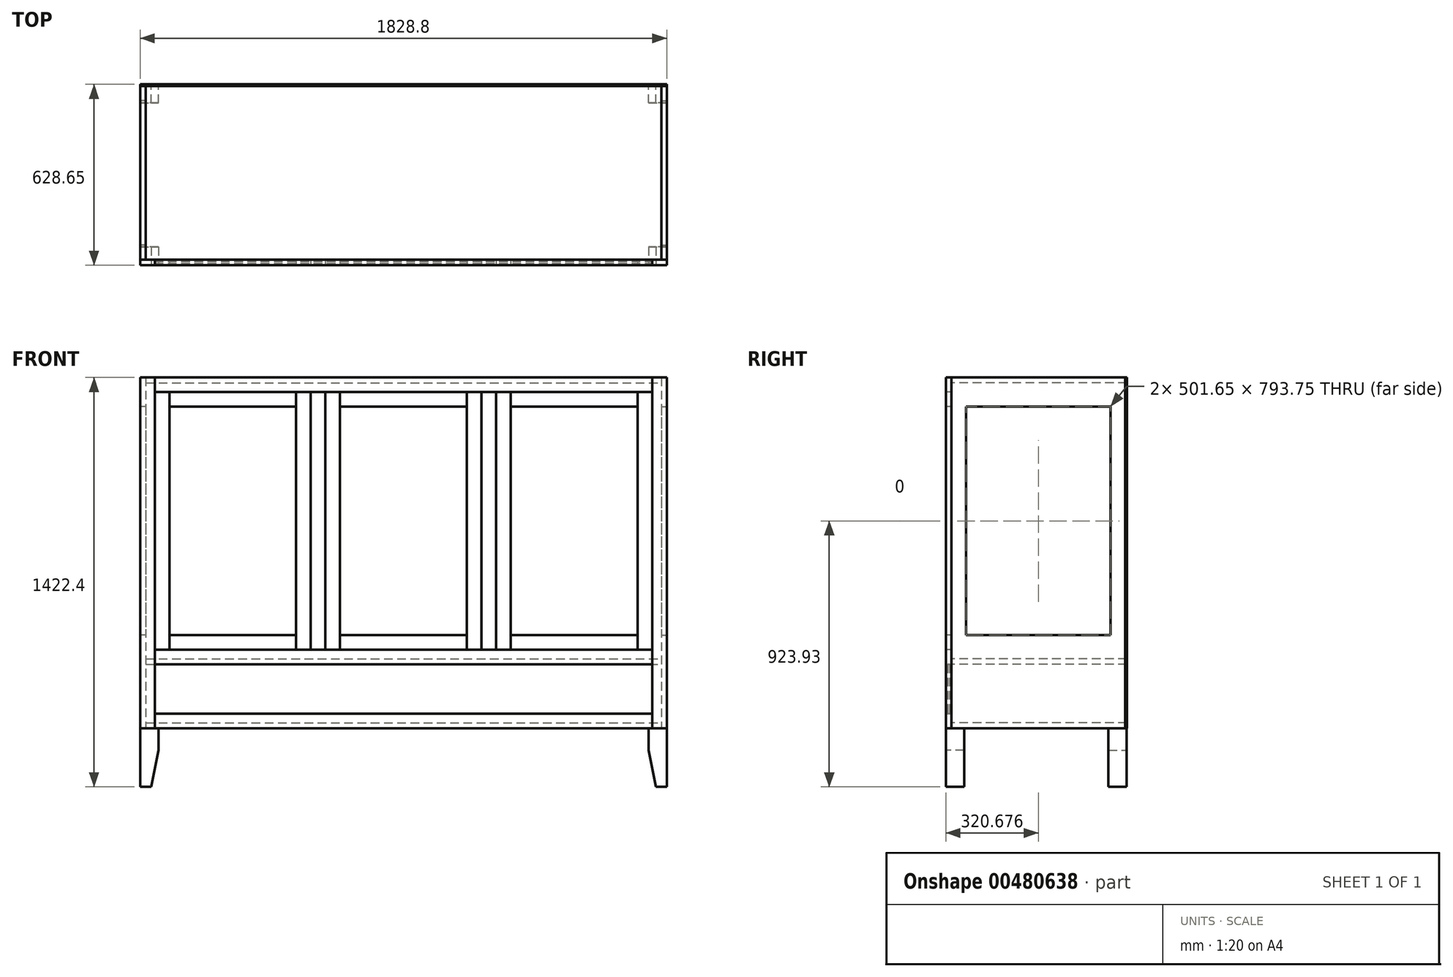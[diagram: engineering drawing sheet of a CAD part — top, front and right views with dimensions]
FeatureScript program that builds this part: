
annotation { "Feature Type Name" : "Feature", "Feature Type Description" : "" }
export const myFeature = defineFeature(function(context is Context, id is Id, definition is map)
    precondition{}
    {
        {
            var Q0;
            Q0=qCreatedBy(makeId("Right.planeOp"),FACE);
            var sketch = newSketch(context, id + "F0", { "sketchPlane" : qUnion([Q0])});
            skLineSegment(sketch, "E0.bottom", {"start": v(-30.46, 1128.18) * mm, "end": v(579.14, 1128.18) * mm});
            skLineSegment(sketch, "E0.top", {"start": v(-30.46, -91.02) * mm, "end": v(579.14, -91.02) * mm});
            skLineSegment(sketch, "E0.left", {"start": v(-30.46, 1128.18) * mm, "end": v(-30.46, -91.02) * mm});
            skLineSegment(sketch, "E0.right", {"start": v(579.14, 1128.18) * mm, "end": v(579.14, -91.02) * mm});
            skSolve(sketch);
        }
        {
            var Q0;
            Q0=qSketchRegion(id+"F0",true);
            extrude(context, id + "F1", {"entities" : qUnion([Q0]), "depth" : 19.05 * mm});
        }
        {
            var Q0;
            Q0=makeQuery(id+"F1.opExtrude","CAP_FACE",FACE,{"disambiguationData":[OSD([sQuery(id+"F0.wireOp",EDGE,"E0.bottom"),sQuery(id+"F0.wireOp",EDGE,"E0.top"),sQuery(id+"F0.wireOp",EDGE,"E0.left"),sQuery(id+"F0.wireOp",EDGE,"E0.right")])],"isStart":false});
            var sketch = newSketch(context, id + "F2", { "sketchPlane" : qUnion([Q0])});
            skLineSegment(sketch, "E1.bottom", {"start": v(20.34, 1026.58) * mm, "end": v(522, 1026.58) * mm});
            skLineSegment(sketch, "E1.top", {"start": v(20.34, 232.83) * mm, "end": v(522, 232.83) * mm});
            skLineSegment(sketch, "E1.left", {"start": v(20.34, 1026.58) * mm, "end": v(20.34, 232.83) * mm});
            skLineSegment(sketch, "E1.right", {"start": v(522, 1026.58) * mm, "end": v(522, 232.83) * mm});
            skSolve(sketch);
        }
        {
            var Q0;
            Q0 = qSketchRegion(id + "F2", true);
            extrude(context, id + "F3", {"entities" : qUnion([Q0]), "operationType" : NewBodyOperationType.REMOVE, "endBound" : BoundingType.THROUGH_ALL, "oppositeDirection" : true, "depth" : 2032 * mm});
        }
        {
            var Q0;
            Q0=makeQuery(id+"F1.opExtrude","CAP_FACE",FACE,{"disambiguationData":[OSD([sQuery(id+"F0.wireOp",EDGE,"E0.bottom"),sQuery(id+"F0.wireOp",EDGE,"E0.top"),sQuery(id+"F0.wireOp",EDGE,"E0.left"),sQuery(id+"F0.wireOp",EDGE,"E0.right")])],"isStart":false});
            cPlane(context, id + "F4", {"entities" : qUnion([Q0]), "cplaneType" : CPlaneType.OFFSET, "offset" : 914.4 * mm, "oppositeDirection" : true, "width" : 152.4 * mm, "height" : 152.4 * mm});
        }
        {
            var Q0;
            Q0=makeQuery(id+"F1.opExtrude","SWEPT_BODY",BODY,{"disambiguationData":[OSD([sQuery(id+"F0.wireOp",EDGE,"E0.bottom"),sQuery(id+"F0.wireOp",EDGE,"E0.top"),sQuery(id+"F0.wireOp",EDGE,"E0.left"),sQuery(id+"F0.wireOp",EDGE,"E0.right")])]});
            var Q1;
            Q1=qCreatedBy(id+"F4.planeOp",FACE);
            mirror(context, id + "F5", {"entities" : qUnion([Q0]), "mirrorPlane" : qUnion([Q1])});
        }
        {
            var Q0;
            Q0=makeQuery(id+"F1.opExtrude","SWEPT_FACE",FACE,{"disambiguationData":[OSD([sQuery(id+"F0.wireOp",EDGE,"E0.left")])]});
            var sketch = newSketch(context, id + "F6", { "sketchPlane" : qUnion([Q0])});
            skLineSegment(sketch, "E2.bottom", {"start": v(-1790.7, 1128.18) * mm, "end": v(0, 1128.18) * mm});
            skLineSegment(sketch, "E2.top", {"start": v(-1790.7, 1109.13) * mm, "end": v(0, 1109.13) * mm});
            skLineSegment(sketch, "E2.left", {"start": v(-1790.7, 1128.18) * mm, "end": v(-1790.7, 1109.13) * mm});
            skLineSegment(sketch, "E2.right", {"start": v(0, 1128.18) * mm, "end": v(0, 1109.13) * mm});
            skSolve(sketch);
        }
        {
            var Q0;
            Q0=qSketchRegion(id+"F6",true);
            extrude(context, id + "F7", {"entities" : qUnion([Q0]), "oppositeDirection" : true, "depth" : 609.6 * mm});
        }
        {
            var Q0;
            Q0=makeQuery(id+"F1.opExtrude","SWEPT_FACE",FACE,{"disambiguationData":[OSD([sQuery(id+"F0.wireOp",EDGE,"E0.left")])]});
            var sketch = newSketch(context, id + "F8", { "sketchPlane" : qUnion([Q0])});
            skLineSegment(sketch, "E3.bottom", {"start": v(-1790.7, -71.97) * mm, "end": v(0, -71.97) * mm});
            skLineSegment(sketch, "E3.top", {"start": v(-1790.7, -91.02) * mm, "end": v(0, -91.02) * mm});
            skLineSegment(sketch, "E3.left", {"start": v(-1790.7, -71.97) * mm, "end": v(-1790.7, -91.02) * mm});
            skLineSegment(sketch, "E3.right", {"start": v(0, -71.97) * mm, "end": v(0, -91.02) * mm});
            skSolve(sketch);
        }
        {
            var Q0;
            Q0=qSketchRegion(id+"F8",true);
            extrude(context, id + "F9", {"entities" : qUnion([Q0]), "oppositeDirection" : true, "depth" : 609.6 * mm});
        }
        {
            var Q0;
            Q0=makeQuery(id+"F1.opExtrude","SWEPT_FACE",FACE,{"disambiguationData":[OSD([sQuery(id+"F0.wireOp",EDGE,"E0.left")])]});
            var sketch = newSketch(context, id + "F10", { "sketchPlane" : qUnion([Q0])});
            skLineSegment(sketch, "E4.bottom", {"start": v(-1790.7, 150.28) * mm, "end": v(0, 150.28) * mm});
            skLineSegment(sketch, "E4.top", {"start": v(-1790.7, 131.23) * mm, "end": v(0, 131.23) * mm});
            skLineSegment(sketch, "E4.left", {"start": v(-1790.7, 150.28) * mm, "end": v(-1790.7, 131.23) * mm});
            skLineSegment(sketch, "E4.right", {"start": v(0, 150.28) * mm, "end": v(0, 131.23) * mm});
            skSolve(sketch);
        }
        {
            var Q0;
            Q0=qSketchRegion(id+"F10",true);
            extrude(context, id + "F11", {"entities" : qUnion([Q0]), "oppositeDirection" : true, "depth" : 609.6 * mm});
        }
        {
            var Q0;
            Q0=makeQuery(id+"F1.opExtrude","SWEPT_FACE",FACE,{"disambiguationData":[OSD([sQuery(id+"F0.wireOp",EDGE,"E0.left")])]});
            var sketch = newSketch(context, id + "F12", { "sketchPlane" : qUnion([Q0])});
            skLineSegment(sketch, "E5.bottom", {"start": v(-31.75, 1128.18) * mm, "end": v(19.05, 1128.18) * mm});
            skLineSegment(sketch, "E5.top", {"start": v(-31.75, -91.02) * mm, "end": v(19.05, -91.02) * mm});
            skLineSegment(sketch, "E5.left", {"start": v(-31.75, 1128.18) * mm, "end": v(-31.75, -91.02) * mm});
            skLineSegment(sketch, "E5.right", {"start": v(19.05, 1128.18) * mm, "end": v(19.05, -91.02) * mm});
            skSolve(sketch);
        }
        {
            var Q0;
            Q0=qSketchRegion(id+"F12",true);
            extrude(context, id + "F13", {"entities" : qUnion([Q0]), "depth" : 19.05 * mm});
        }
        {
            var Q0;
            Q0=makeQuery(id+"F13.opExtrude","SWEPT_BODY",BODY,{"disambiguationData":[OSD([sQuery(id+"F12.wireOp",EDGE,"E5.bottom"),sQuery(id+"F12.wireOp",EDGE,"E5.top"),sQuery(id+"F12.wireOp",EDGE,"E5.left"),sQuery(id+"F12.wireOp",EDGE,"E5.right")])]});
            var Q1;
            Q1=qCreatedBy(id+"F4.planeOp",FACE);
            mirror(context, id + "F14", {"entities" : qUnion([Q0]), "mirrorPlane" : qUnion([Q1])});
        }
        {
            var Q0;
            Q0=makeQuery(id+"F7.opExtrude","CAP_FACE",FACE,{"disambiguationData":[OSD([sQuery(id+"F6.wireOp",EDGE,"E2.bottom"),sQuery(id+"F6.wireOp",EDGE,"E2.top"),sQuery(id+"F6.wireOp",EDGE,"E2.left"),sQuery(id+"F6.wireOp",EDGE,"E2.right")])],"isStart":true});
            var sketch = newSketch(context, id + "F15", { "sketchPlane" : qUnion([Q0])});
            skLineSegment(sketch, "E6.bottom", {"start": v(-1758.95, 1128.18) * mm, "end": v(-31.75, 1128.18) * mm});
            skLineSegment(sketch, "E6.top", {"start": v(-1758.95, 1077.38) * mm, "end": v(-31.75, 1077.38) * mm});
            skLineSegment(sketch, "E6.left", {"start": v(-1758.95, 1128.18) * mm, "end": v(-1758.95, 1077.38) * mm});
            skLineSegment(sketch, "E6.right", {"start": v(-31.75, 1128.18) * mm, "end": v(-31.75, 1077.38) * mm});
            skSolve(sketch);
        }
        {
            var Q0;
            Q0=qSketchRegion(id+"F15",true);
            extrude(context, id + "F16", {"entities" : qUnion([Q0]), "depth" : 19.05 * mm});
        }
        {
            var Q0;
            Q0=makeQuery(id+"F11.opExtrude","CAP_FACE",FACE,{"disambiguationData":[OSD([sQuery(id+"F10.wireOp",EDGE,"E4.bottom"),sQuery(id+"F10.wireOp",EDGE,"E4.top"),sQuery(id+"F10.wireOp",EDGE,"E4.left"),sQuery(id+"F10.wireOp",EDGE,"E4.right")])],"isStart":true});
            var sketch = newSketch(context, id + "F17", { "sketchPlane" : qUnion([Q0])});
            skLineSegment(sketch, "E7.bottom", {"start": v(-1758.95, 182.03) * mm, "end": v(-31.75, 182.03) * mm});
            skLineSegment(sketch, "E7.top", {"start": v(-1758.95, 131.23) * mm, "end": v(-31.75, 131.23) * mm});
            skLineSegment(sketch, "E7.left", {"start": v(-1758.95, 182.03) * mm, "end": v(-1758.95, 131.23) * mm});
            skLineSegment(sketch, "E7.right", {"start": v(-31.75, 182.03) * mm, "end": v(-31.75, 131.23) * mm});
            skSolve(sketch);
        }
        {
            var Q0;
            Q0=qSketchRegion(id+"F17",true);
            extrude(context, id + "F18", {"entities" : qUnion([Q0]), "depth" : 19.05 * mm});
        }
        {
            var Q0;
            Q0=makeQuery(id+"F9.opExtrude","CAP_FACE",FACE,{"disambiguationData":[OSD([sQuery(id+"F8.wireOp",EDGE,"E3.bottom"),sQuery(id+"F8.wireOp",EDGE,"E3.top"),sQuery(id+"F8.wireOp",EDGE,"E3.left"),sQuery(id+"F8.wireOp",EDGE,"E3.right")])],"isStart":true});
            var sketch = newSketch(context, id + "F19", { "sketchPlane" : qUnion([Q0])});
            skLineSegment(sketch, "E8.bottom", {"start": v(-1758.95, -91.02) * mm, "end": v(-31.75, -91.02) * mm});
            skLineSegment(sketch, "E8.top", {"start": v(-1758.95, -40.22) * mm, "end": v(-31.75, -40.22) * mm});
            skLineSegment(sketch, "E8.left", {"start": v(-1758.95, -91.02) * mm, "end": v(-1758.95, -40.22) * mm});
            skLineSegment(sketch, "E8.right", {"start": v(-31.75, -91.02) * mm, "end": v(-31.75, -40.22) * mm});
            skSolve(sketch);
        }
        {
            var Q0;
            Q0=qSketchRegion(id+"F19",true);
            extrude(context, id + "F20", {"entities" : qUnion([Q0]), "depth" : 19.05 * mm});
        }
        {
            var Q0;
            Q0=makeQuery(id+"F14.opPattern","COPY",FACE,{"derivedFrom":makeQuery(id+"F13.opExtrude","CAP_FACE",FACE,{"disambiguationData":[OSD([sQuery(id+"F12.wireOp",EDGE,"E5.bottom"),sQuery(id+"F12.wireOp",EDGE,"E5.top"),sQuery(id+"F12.wireOp",EDGE,"E5.left"),sQuery(id+"F12.wireOp",EDGE,"E5.right")])],"isStart":false}),"instanceName":"1"});
            cPlane(context, id + "F21", {"entities" : qUnion([Q0]), "cplaneType" : CPlaneType.OFFSET, "offset" : 6.35 * mm, "oppositeDirection" : true, "width" : 152.4 * mm, "height" : 152.4 * mm});
        }
        {
            var Q0;
            Q0=qCreatedBy(id+"F21.planeOp",FACE);
            var sketch = newSketch(context, id + "F22", { "sketchPlane" : qUnion([Q0])});
            skLineSegment(sketch, "E9.bottom", {"start": v(-1758.95, 131.23) * mm, "end": v(-31.75, 131.23) * mm});
            skLineSegment(sketch, "E9.top", {"start": v(-1758.95, -40.22) * mm, "end": v(-31.75, -40.22) * mm});
            skLineSegment(sketch, "E9.left", {"start": v(-1758.95, 131.23) * mm, "end": v(-1758.95, -40.22) * mm});
            skLineSegment(sketch, "E9.right", {"start": v(-31.75, 131.23) * mm, "end": v(-31.75, -40.22) * mm});
            skSolve(sketch);
        }
        {
            var Q0;
            Q0=makeQuery(id+"F16.opExtrude","CAP_FACE",FACE,{"disambiguationData":[OSD([sQuery(id+"F15.wireOp",EDGE,"E6.bottom"),sQuery(id+"F15.wireOp",EDGE,"E6.top"),sQuery(id+"F15.wireOp",EDGE,"E6.left"),sQuery(id+"F15.wireOp",EDGE,"E6.right")])],"isStart":false});
            var sketch = newSketch(context, id + "F23", { "sketchPlane" : qUnion([Q0])});
            skLineSegment(sketch, "E10.bottom", {"start": v(-624.33, 1077.38) * mm, "end": v(-573.53, 1077.38) * mm});
            skLineSegment(sketch, "E10.top", {"start": v(-624.33, 182.03) * mm, "end": v(-573.53, 182.03) * mm});
            skLineSegment(sketch, "E10.left", {"start": v(-624.33, 1077.38) * mm, "end": v(-624.33, 182.03) * mm});
            skLineSegment(sketch, "E10.right", {"start": v(-573.53, 1077.38) * mm, "end": v(-573.53, 182.03) * mm});
            skSolve(sketch);
        }
        {
            var Q0;
            Q0=qSketchRegion(id+"F23",true);
            extrude(context, id + "F24", {"entities" : qUnion([Q0]), "oppositeDirection" : true, "depth" : 19.05 * mm});
        }
        {
            var Q0;
            Q0=makeQuery(id+"F24.opExtrude","SWEPT_BODY",BODY,{"disambiguationData":[OSD([sQuery(id+"F23.wireOp",EDGE,"E10.bottom"),sQuery(id+"F23.wireOp",EDGE,"E10.top"),sQuery(id+"F23.wireOp",EDGE,"E10.left"),sQuery(id+"F23.wireOp",EDGE,"E10.right")])]});
            var Q1;
            Q1=qCreatedBy(id+"F4.planeOp",FACE);
            mirror(context, id + "F25", {"entities" : qUnion([Q0]), "mirrorPlane" : qUnion([Q1])});
        }
        {
            var Q0;
            Q0=qSketchRegion(id+"F22",true);
            extrude(context, id + "F26", {"entities" : qUnion([Q0]), "oppositeDirection" : true, "depth" : 6.35 * mm});
        }
        {
            var Q0;
            Q0=makeQuery(id+"F16.opExtrude","CAP_FACE",FACE,{"disambiguationData":[OSD([sQuery(id+"F15.wireOp",EDGE,"E6.bottom"),sQuery(id+"F15.wireOp",EDGE,"E6.top"),sQuery(id+"F15.wireOp",EDGE,"E6.left"),sQuery(id+"F15.wireOp",EDGE,"E6.right")])],"isStart":false});
            var sketch = newSketch(context, id + "F27", { "sketchPlane" : qUnion([Q0])});
            skLineSegment(sketch, "E11.bottom", {"start": v(-82.55, 1077.38) * mm, "end": v(-31.75, 1077.38) * mm});
            skLineSegment(sketch, "E11.top", {"start": v(-82.55, 182.03) * mm, "end": v(-31.75, 182.03) * mm});
            skLineSegment(sketch, "E11.left", {"start": v(-82.55, 1077.38) * mm, "end": v(-82.55, 182.03) * mm});
            skLineSegment(sketch, "E11.right", {"start": v(-31.75, 1077.38) * mm, "end": v(-31.75, 182.03) * mm});
            skSolve(sketch);
        }
        {
            var Q0;
            Q0=qSketchRegion(id+"F27",true);
            extrude(context, id + "F28", {"entities" : qUnion([Q0]), "oppositeDirection" : true, "depth" : 19.05 * mm});
        }
        {
            var Q0;
            Q0=makeQuery(id+"F28.opExtrude","CAP_FACE",FACE,{"disambiguationData":[OSD([sQuery(id+"F27.wireOp",EDGE,"E11.bottom"),sQuery(id+"F27.wireOp",EDGE,"E11.top"),sQuery(id+"F27.wireOp",EDGE,"E11.left"),sQuery(id+"F27.wireOp",EDGE,"E11.right")])],"isStart":true});
            var sketch = newSketch(context, id + "F29", { "sketchPlane" : qUnion([Q0])});
            skLineSegment(sketch, "E12.bottom", {"start": v(-573.53, 1077.38) * mm, "end": v(-522.73, 1077.38) * mm});
            skLineSegment(sketch, "E12.top", {"start": v(-573.53, 182.03) * mm, "end": v(-522.73, 182.03) * mm});
            skLineSegment(sketch, "E12.left", {"start": v(-573.53, 1077.38) * mm, "end": v(-573.53, 182.03) * mm});
            skLineSegment(sketch, "E12.right", {"start": v(-522.73, 1077.38) * mm, "end": v(-522.73, 182.03) * mm});
            skSolve(sketch);
        }
        {
            var Q0;
            Q0=qSketchRegion(id+"F29",true);
            extrude(context, id + "F30", {"entities" : qUnion([Q0]), "oppositeDirection" : true, "depth" : 19.05 * mm});
        }
        {
            var Q0;
            Q0=makeQuery(id+"F28.opExtrude","CAP_FACE",FACE,{"disambiguationData":[OSD([sQuery(id+"F27.wireOp",EDGE,"E11.bottom"),sQuery(id+"F27.wireOp",EDGE,"E11.top"),sQuery(id+"F27.wireOp",EDGE,"E11.left"),sQuery(id+"F27.wireOp",EDGE,"E11.right")])],"isStart":true});
            var sketch = newSketch(context, id + "F31", { "sketchPlane" : qUnion([Q0])});
            skLineSegment(sketch, "E13.bottom", {"start": v(-522.73, 1077.38) * mm, "end": v(-82.55, 1077.38) * mm});
            skLineSegment(sketch, "E13.top", {"start": v(-522.73, 1026.58) * mm, "end": v(-82.55, 1026.58) * mm});
            skLineSegment(sketch, "E13.left", {"start": v(-522.73, 1077.38) * mm, "end": v(-522.73, 1026.58) * mm});
            skLineSegment(sketch, "E13.right", {"start": v(-82.55, 1077.38) * mm, "end": v(-82.55, 1026.58) * mm});
            skSolve(sketch);
        }
        {
            var Q0;
            Q0=qSketchRegion(id+"F31",true);
            extrude(context, id + "F32", {"entities" : qUnion([Q0]), "oppositeDirection" : true, "depth" : 19.05 * mm});
        }
        {
            var Q0;
            Q0=makeQuery(id+"F28.opExtrude","CAP_FACE",FACE,{"disambiguationData":[OSD([sQuery(id+"F27.wireOp",EDGE,"E11.bottom"),sQuery(id+"F27.wireOp",EDGE,"E11.top"),sQuery(id+"F27.wireOp",EDGE,"E11.left"),sQuery(id+"F27.wireOp",EDGE,"E11.right")])],"isStart":true});
            var sketch = newSketch(context, id + "F33", { "sketchPlane" : qUnion([Q0])});
            skLineSegment(sketch, "E14.bottom", {"start": v(-522.73, 232.83) * mm, "end": v(-82.55, 232.83) * mm});
            skLineSegment(sketch, "E14.top", {"start": v(-522.73, 182.03) * mm, "end": v(-82.55, 182.03) * mm});
            skLineSegment(sketch, "E14.left", {"start": v(-522.73, 232.83) * mm, "end": v(-522.73, 182.03) * mm});
            skLineSegment(sketch, "E14.right", {"start": v(-82.55, 232.83) * mm, "end": v(-82.55, 182.03) * mm});
            skSolve(sketch);
        }
        {
            var Q0;
            Q0=qSketchRegion(id+"F33",true);
            extrude(context, id + "F34", {"entities" : qUnion([Q0]), "oppositeDirection" : true, "depth" : 19.05 * mm});
        }
        {
            var Q0;
            Q0=makeQuery(id+"F30.opExtrude","SWEPT_BODY",BODY,{"disambiguationData":[OSD([sQuery(id+"F29.wireOp",EDGE,"E12.bottom"),sQuery(id+"F29.wireOp",EDGE,"E12.top"),sQuery(id+"F29.wireOp",EDGE,"E12.left"),sQuery(id+"F29.wireOp",EDGE,"E12.right")])]});
            var Q1;
            Q1=makeQuery(id+"F32.opExtrude","SWEPT_BODY",BODY,{"disambiguationData":[OSD([sQuery(id+"F31.wireOp",EDGE,"E13.bottom"),sQuery(id+"F31.wireOp",EDGE,"E13.top"),sQuery(id+"F31.wireOp",EDGE,"E13.left"),sQuery(id+"F31.wireOp",EDGE,"E13.right")])]});
            var Q2;
            Q2=makeQuery(id+"F28.opExtrude","SWEPT_BODY",BODY,{"disambiguationData":[OSD([sQuery(id+"F27.wireOp",EDGE,"E11.bottom"),sQuery(id+"F27.wireOp",EDGE,"E11.top"),sQuery(id+"F27.wireOp",EDGE,"E11.left"),sQuery(id+"F27.wireOp",EDGE,"E11.right")])]});
            var Q3;
            Q3=makeQuery(id+"F34.opExtrude","SWEPT_BODY",BODY,{"disambiguationData":[OSD([sQuery(id+"F33.wireOp",EDGE,"E14.bottom"),sQuery(id+"F33.wireOp",EDGE,"E14.top"),sQuery(id+"F33.wireOp",EDGE,"E14.left"),sQuery(id+"F33.wireOp",EDGE,"E14.right")])]});
            var Q4;
            Q4=qCreatedBy(id+"F4.planeOp",FACE);
            mirror(context, id + "F35", {"entities" : qUnion([Q0, Q1, Q2, Q3]), "mirrorPlane" : qUnion([Q4])});
        }
        {
            var Q0;
            Q0=makeQuery(id+"F24.opExtrude","CAP_FACE",FACE,{"disambiguationData":[OSD([sQuery(id+"F23.wireOp",EDGE,"E10.bottom"),sQuery(id+"F23.wireOp",EDGE,"E10.top"),sQuery(id+"F23.wireOp",EDGE,"E10.left"),sQuery(id+"F23.wireOp",EDGE,"E10.right")])],"isStart":true});
            var sketch = newSketch(context, id + "F36", { "sketchPlane" : qUnion([Q0])});
            skLineSegment(sketch, "E15.bottom", {"start": v(-675.13, 1077.38) * mm, "end": v(-624.33, 1077.38) * mm});
            skLineSegment(sketch, "E15.top", {"start": v(-675.13, 182.03) * mm, "end": v(-624.33, 182.03) * mm});
            skLineSegment(sketch, "E15.left", {"start": v(-675.13, 1077.38) * mm, "end": v(-675.13, 182.03) * mm});
            skLineSegment(sketch, "E15.right", {"start": v(-624.33, 1077.38) * mm, "end": v(-624.33, 182.03) * mm});
            skSolve(sketch);
        }
        {
            var Q0;
            Q0=qSketchRegion(id+"F36",true);
            extrude(context, id + "F37", {"entities" : qUnion([Q0]), "oppositeDirection" : true, "depth" : 19.05 * mm});
        }
        {
            var Q0;
            Q0=makeQuery(id+"F37.opExtrude","CAP_FACE",FACE,{"disambiguationData":[OSD([sQuery(id+"F36.wireOp",EDGE,"E15.bottom"),sQuery(id+"F36.wireOp",EDGE,"E15.top"),sQuery(id+"F36.wireOp",EDGE,"E15.left"),sQuery(id+"F36.wireOp",EDGE,"E15.right")])],"isStart":true});
            var sketch = newSketch(context, id + "F38", { "sketchPlane" : qUnion([Q0])});
            skLineSegment(sketch, "E16.bottom", {"start": v(-1166.37, 1077.38) * mm, "end": v(-1115.57, 1077.38) * mm});
            skLineSegment(sketch, "E16.top", {"start": v(-1166.37, 182.03) * mm, "end": v(-1115.57, 182.03) * mm});
            skLineSegment(sketch, "E16.left", {"start": v(-1166.37, 1077.38) * mm, "end": v(-1166.37, 182.03) * mm});
            skLineSegment(sketch, "E16.right", {"start": v(-1115.57, 1077.38) * mm, "end": v(-1115.57, 182.03) * mm});
            skSolve(sketch);
        }
        {
            var Q0;
            Q0=qSketchRegion(id+"F38",true);
            extrude(context, id + "F39", {"entities" : qUnion([Q0]), "oppositeDirection" : true, "depth" : 19.05 * mm});
        }
        {
            var Q0;
            Q0=makeQuery(id+"F37.opExtrude","CAP_FACE",FACE,{"disambiguationData":[OSD([sQuery(id+"F36.wireOp",EDGE,"E15.bottom"),sQuery(id+"F36.wireOp",EDGE,"E15.top"),sQuery(id+"F36.wireOp",EDGE,"E15.left"),sQuery(id+"F36.wireOp",EDGE,"E15.right")])],"isStart":true});
            var sketch = newSketch(context, id + "F40", { "sketchPlane" : qUnion([Q0])});
            skLineSegment(sketch, "E17.bottom", {"start": v(-1115.57, 1077.38) * mm, "end": v(-675.13, 1077.38) * mm});
            skLineSegment(sketch, "E17.top", {"start": v(-1115.57, 1026.58) * mm, "end": v(-675.13, 1026.58) * mm});
            skLineSegment(sketch, "E17.left", {"start": v(-1115.57, 1077.38) * mm, "end": v(-1115.57, 1026.58) * mm});
            skLineSegment(sketch, "E17.right", {"start": v(-675.13, 1077.38) * mm, "end": v(-675.13, 1026.58) * mm});
            skSolve(sketch);
        }
        {
            var Q0;
            Q0=qSketchRegion(id+"F40",true);
            extrude(context, id + "F41", {"entities" : qUnion([Q0]), "oppositeDirection" : true, "depth" : 19.05 * mm});
        }
        {
            var Q0;
            Q0=makeQuery(id+"F37.opExtrude","CAP_FACE",FACE,{"disambiguationData":[OSD([sQuery(id+"F36.wireOp",EDGE,"E15.bottom"),sQuery(id+"F36.wireOp",EDGE,"E15.top"),sQuery(id+"F36.wireOp",EDGE,"E15.left"),sQuery(id+"F36.wireOp",EDGE,"E15.right")])],"isStart":true});
            var sketch = newSketch(context, id + "F42", { "sketchPlane" : qUnion([Q0])});
            skLineSegment(sketch, "E18.bottom", {"start": v(-1115.57, 232.83) * mm, "end": v(-675.13, 232.83) * mm});
            skLineSegment(sketch, "E18.top", {"start": v(-1115.57, 182.03) * mm, "end": v(-675.13, 182.03) * mm});
            skLineSegment(sketch, "E18.left", {"start": v(-1115.57, 232.83) * mm, "end": v(-1115.57, 182.03) * mm});
            skLineSegment(sketch, "E18.right", {"start": v(-675.13, 232.83) * mm, "end": v(-675.13, 182.03) * mm});
            skSolve(sketch);
        }
        {
            var Q0;
            Q0=qSketchRegion(id+"F42",true);
            extrude(context, id + "F43", {"entities" : qUnion([Q0]), "oppositeDirection" : true, "depth" : 19.05 * mm});
        }
        {
            var Q0;
            Q0=makeQuery(id+"F7.opExtrude","CAP_FACE",FACE,{"disambiguationData":[OSD([sQuery(id+"F6.wireOp",EDGE,"E2.bottom"),sQuery(id+"F6.wireOp",EDGE,"E2.top"),sQuery(id+"F6.wireOp",EDGE,"E2.left"),sQuery(id+"F6.wireOp",EDGE,"E2.right")])],"isStart":false});
            var sketch = newSketch(context, id + "F44", { "sketchPlane" : qUnion([Q0])});
            skLineSegment(sketch, "E19.bottom", {"start": v(-19.05, 1128.18) * mm, "end": v(1809.75, 1128.18) * mm});
            skLineSegment(sketch, "E19.top", {"start": v(-19.05, -91.02) * mm, "end": v(1809.75, -91.02) * mm});
            skLineSegment(sketch, "E19.left", {"start": v(-19.05, 1128.18) * mm, "end": v(-19.05, -91.02) * mm});
            skLineSegment(sketch, "E19.right", {"start": v(1809.75, 1128.18) * mm, "end": v(1809.75, -91.02) * mm});
            skSolve(sketch);
        }
        {
            var Q0;
            Q0=qSketchRegion(id+"F44",true);
            extrude(context, id + "F45", {"entities" : qUnion([Q0]), "oppositeDirection" : true, "depth" : 6.35 * mm});
        }
        {
            var Q0;
            Q0=makeQuery(id+"F13.opExtrude","CAP_FACE",FACE,{"disambiguationData":[OSD([sQuery(id+"F12.wireOp",EDGE,"E5.bottom"),sQuery(id+"F12.wireOp",EDGE,"E5.top"),sQuery(id+"F12.wireOp",EDGE,"E5.left"),sQuery(id+"F12.wireOp",EDGE,"E5.right")])],"isStart":false});
            var sketch = newSketch(context, id + "F46", { "sketchPlane" : qUnion([Q0])});
            skLineSegment(sketch, "E20", {"start": v(19.05, -91.02) * mm, "end": v(19.05, -294.22) * mm});
            skLineSegment(sketch, "E21", {"start": v(19.05, -294.22) * mm, "end": v(-19.05, -294.22) * mm});
            skLineSegment(sketch, "E22", {"start": v(-19.05, -294.22) * mm, "end": v(-44.45, -167.22) * mm});
            skLineSegment(sketch, "E23", {"start": v(-44.45, -167.22) * mm, "end": v(-44.45, -91.02) * mm});
            skLineSegment(sketch, "E24", {"start": v(-44.45, -91.02) * mm, "end": v(19.05, -91.02) * mm});
            skSolve(sketch);
        }
        {
            var Q0;
            Q0=qSketchRegion(id+"F46",true);
            extrude(context, id + "F47", {"entities" : qUnion([Q0]), "oppositeDirection" : true, "depth" : 63.5 * mm});
        }
        {
            var Q0;
            Q0=makeQuery(id+"F47.opExtrude","SWEPT_BODY",BODY,{"disambiguationData":[OSD([sQuery(id+"F46.wireOp",EDGE,"E20"),sQuery(id+"F46.wireOp",EDGE,"E21"),sQuery(id+"F46.wireOp",EDGE,"E22"),sQuery(id+"F46.wireOp",EDGE,"E23"),sQuery(id+"F46.wireOp",EDGE,"E24")])]});
            var Q1;
            Q1=qCreatedBy(id+"F4.planeOp",FACE);
            mirror(context, id + "F48", {"entities" : qUnion([Q0]), "mirrorPlane" : qUnion([Q1])});
        }
        {
            var Q0;
            Q0=makeQuery(id+"F7.opExtrude","CAP_FACE",FACE,{"disambiguationData":[OSD([sQuery(id+"F6.wireOp",EDGE,"E2.bottom"),sQuery(id+"F6.wireOp",EDGE,"E2.top"),sQuery(id+"F6.wireOp",EDGE,"E2.left"),sQuery(id+"F6.wireOp",EDGE,"E2.right")])],"isStart":false});
            cPlane(context, id + "F49", {"entities" : qUnion([Q0]), "cplaneType" : CPlaneType.OFFSET, "offset" : 314.96 * mm, "oppositeDirection" : true, "width" : 152.4 * mm, "height" : 152.4 * mm});
        }
        {
            var Q0;
            Q0=makeQuery(id+"F48.opPattern","COPY",BODY,{"derivedFrom":makeQuery(id+"F47.opExtrude","SWEPT_BODY",BODY,{"disambiguationData":[OSD([sQuery(id+"F46.wireOp",EDGE,"E20"),sQuery(id+"F46.wireOp",EDGE,"E21"),sQuery(id+"F46.wireOp",EDGE,"E22"),sQuery(id+"F46.wireOp",EDGE,"E23"),sQuery(id+"F46.wireOp",EDGE,"E24")])]}),"instanceName":"1"});
            var Q1;
            Q1=makeQuery(id+"F47.opExtrude","SWEPT_BODY",BODY,{"disambiguationData":[OSD([sQuery(id+"F46.wireOp",EDGE,"E20"),sQuery(id+"F46.wireOp",EDGE,"E21"),sQuery(id+"F46.wireOp",EDGE,"E22"),sQuery(id+"F46.wireOp",EDGE,"E23"),sQuery(id+"F46.wireOp",EDGE,"E24")])]});
            var Q2;
            Q2=qCreatedBy(id+"F49.planeOp",FACE);
            mirror(context, id + "F50", {"entities" : qUnion([Q0, Q1]), "mirrorPlane" : qUnion([Q2])});
        }
    });
